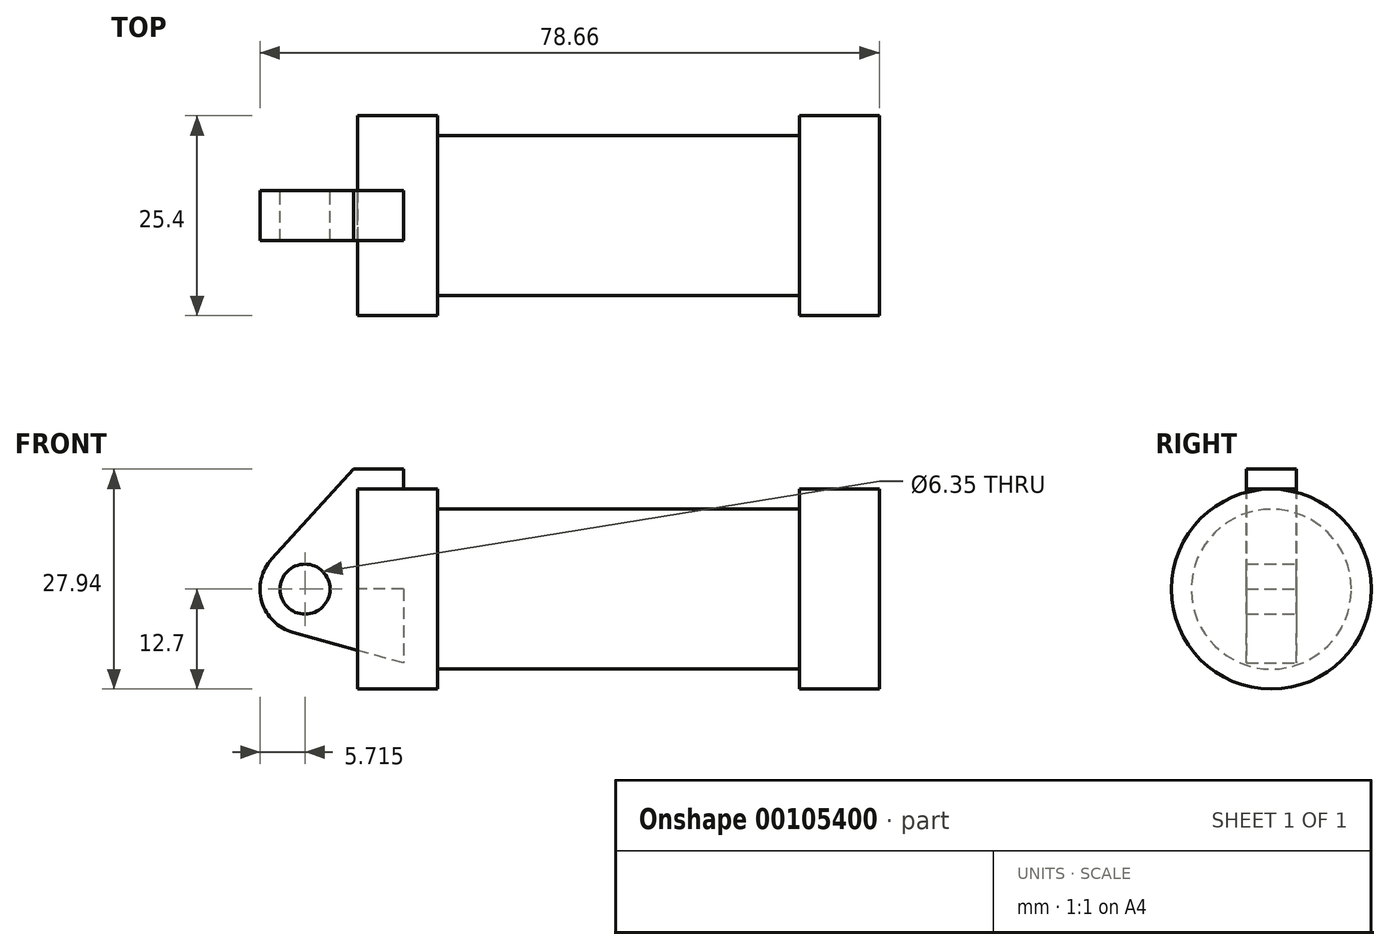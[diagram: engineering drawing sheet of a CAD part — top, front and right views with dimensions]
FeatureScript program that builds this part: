
annotation { "Feature Type Name" : "Feature", "Feature Type Description" : "" }
export const myFeature = defineFeature(function(context is Context, id is Id, definition is map)
    precondition{}
    {
        {
            var Q0;
            Q0=qCreatedBy(makeId("Front.planeOp"),FACE);
            var sketch = newSketch(context, id + "F0", { "sketchPlane" : qUnion([Q0])});
            skLineSegment(sketch, "E0", {"start": v(0, 0) * mm, "end": v(0, 12.7) * mm});
            skLineSegment(sketch, "E1", {"start": v(0, 12.7) * mm, "end": v(10.16, 12.7) * mm});
            skLineSegment(sketch, "E2", {"start": v(10.16, 12.7) * mm, "end": v(10.16, 10.16) * mm});
            skLineSegment(sketch, "E3", {"start": v(10.16, 10.16) * mm, "end": v(56.13, 10.16) * mm});
            skLineSegment(sketch, "E4", {"start": v(56.13, 10.16) * mm, "end": v(56.13, 12.7) * mm});
            skLineSegment(sketch, "E5", {"start": v(56.13, 12.7) * mm, "end": v(66.3, 12.7) * mm});
            skLineSegment(sketch, "E6", {"start": v(66.3, 12.7) * mm, "end": v(66.3, 0) * mm});
            skLineSegment(sketch, "E7", {"start": v(66.3, 0) * mm, "end": v(0, 0) * mm});
            skLineSegment(sketch, "E8", {"start": v(5.84, 15.24) * mm, "end": v(-0.5, 15.24) * mm});
            skLineSegment(sketch, "E9", {"start": v(-0.5, 15.24) * mm, "end": v(-10.88, 3.85) * mm});
            skLineSegment(sketch, "E10", {"start": v(0, 0) * mm, "end": v(-6.65, 0) * mm});
            skCircle(sketch, "E11", {"center": v(-6.65, 0) * mm, "radius": 5.72 * mm});
            skCircle(sketch, "E12", {"center": v(-6.65, 0) * mm, "radius": 3.18 * mm});
            skLineSegment(sketch, "E13", {"start": v(5.84, 15.24) * mm, "end": v(5.84, -9.4) * mm});
            skLineSegment(sketch, "E14", {"start": v(5.84, -9.4) * mm, "end": v(-8.18, -5.5) * mm});
            skSolve(sketch);
        }
        {
            var Q0;
            {var subQ3=sQuery(id+"F0.wireOp",EDGE,"E0");Q0=makeQuery(id+"F0.imprint","IMPRINT",FACE,{"disambiguationData":[TD([[makeQuery(id+"F0.imprint","IMPRINT",EDGE,{"derivedFrom":subQ3}),1.0]])]});}
            var Q1;
            {var subQ4=sQuery(id+"F0.wireOp",EDGE,"E12");Q1=makeQuery(id+"F0.imprint","IMPRINT",FACE,{"disambiguationData":[TD([[makeQuery(id+"F0.imprint","IMPRINT",EDGE,{"derivedFrom":subQ4}),-1.0]])]});}
            var Q2;
            {var subQ0=sQuery(id+"F0.wireOp",EDGE,"E14");Q2=makeQuery(id+"F0.imprint","IMPRINT",FACE,{"disambiguationData":[TD([[makeQuery(id+"F0.imprint","IMPRINT",EDGE,{"derivedFrom":subQ0}),-1.0]])]});}
            extrude(context, id + "F1", {"entities" : qUnion([Q0, Q1, Q2]), "endBound" : BoundingType.SYMMETRIC, "depth" : 6.35 * mm});
        }
        {
            var Q0;
            {var subQ0=sQuery(id+"F0.wireOp",EDGE,"E2");Q0=makeQuery(id+"F0.imprint","IMPRINT",FACE,{"disambiguationData":[TD([[makeQuery(id+"F0.imprint","IMPRINT",EDGE,{"derivedFrom":subQ0}),-1.0]])]});}
            var Q1;
            {var subQ0=sQuery(id+"F0.wireOp",EDGE,"E0");Q1=makeQuery(id+"F0.imprint","IMPRINT",FACE,{"disambiguationData":[TD([[makeQuery(id+"F0.imprint","IMPRINT",EDGE,{"derivedFrom":subQ0}),-1.0]])]});}
            var Q2;
            Q2=sQuery(id+"F0.wireOp",EDGE,"E7");
            revolve(context, id + "F2", {"entities" : qUnion([Q0, Q1]), "axis" : qUnion([Q2]), "revolveType" : RevolveType.FULL});
        }
    });
